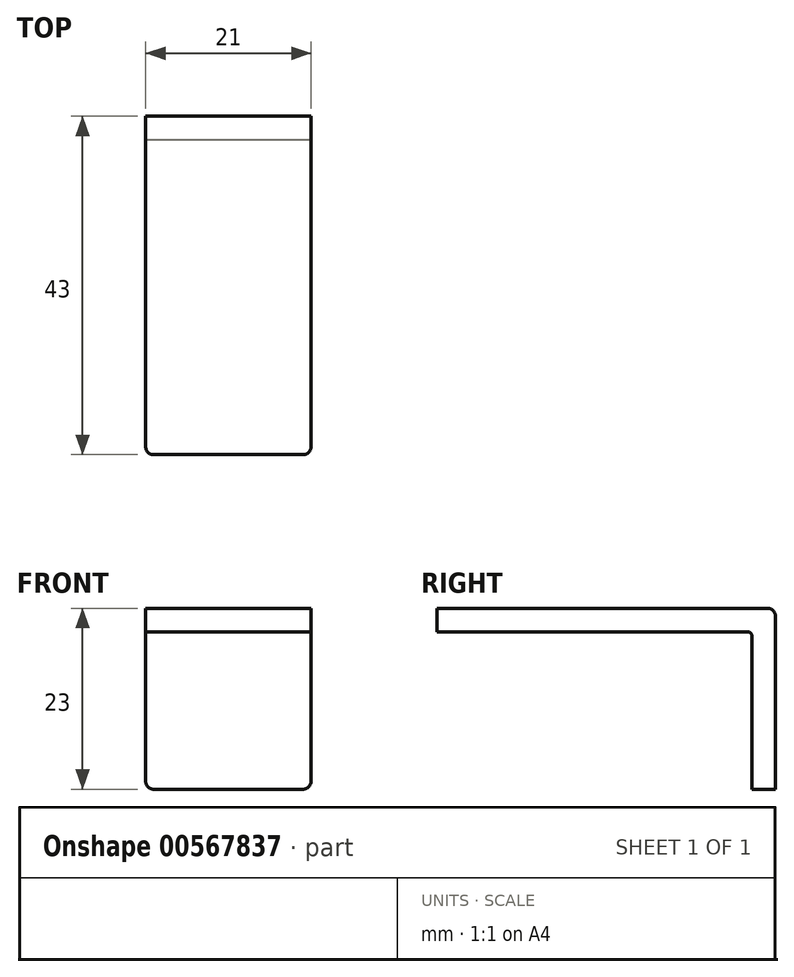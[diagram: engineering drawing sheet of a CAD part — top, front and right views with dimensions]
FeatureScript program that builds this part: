
annotation { "Feature Type Name" : "Feature", "Feature Type Description" : "" }
export const myFeature = defineFeature(function(context is Context, id is Id, definition is map)
    precondition{}
    {
        {
            var Q0;
            Q0=qCreatedBy(makeId("Right.planeOp"),FACE);
            var sketch = newSketch(context, id + "F0", { "sketchPlane" : qUnion([Q0])});
            skLineSegment(sketch, "E0", {"start": v(-40, 0) * mm, "end": v(0, 0) * mm});
            skLineSegment(sketch, "E1", {"start": v(0, 0) * mm, "end": v(0, -20) * mm});
            skLineSegment(sketch, "E2.0", {"start": v(3, 3) * mm, "end": v(3, -20) * mm});
            skLineSegment(sketch, "E2.1", {"start": v(-40, 3) * mm, "end": v(3, 3) * mm});
            skLineSegment(sketch, "E3", {"start": v(-40, 0) * mm, "end": v(-40, 3) * mm});
            skLineSegment(sketch, "E4", {"start": v(0, -20) * mm, "end": v(3, -20) * mm});
            skSolve(sketch);
        }
        {
            var Q0;
            Q0 = qSketchRegion(id + "F0", true);
            extrude(context, id + "F1", {"entities" : qUnion([Q0]), "depth" : 21 * mm, "offsetDistance" : 25 * mm});
        }
        {
            var Q0;
            Q0=makeQuery(id+"F1.opExtrude","SWEPT_EDGE",EDGE,{"disambiguationData":[OSD([sQuery(id+"F0.wireOp",EDGE,"E2.0"),sQuery(id+"F0.wireOp",EDGE,"E2.1")])]});
            var Q1;
            Q1=makeQuery(id+"F1.opExtrude","CAP_EDGE",EDGE,{"disambiguationData":[OSD([sQuery(id+"F0.wireOp",EDGE,"E3")])],"isStart":false});
            var Q2;
            Q2=makeQuery(id+"F1.opExtrude","CAP_EDGE",EDGE,{"disambiguationData":[OSD([sQuery(id+"F0.wireOp",EDGE,"E3")])],"isStart":true});
            var Q3;
            Q3=makeQuery(id+"F1.opExtrude","CAP_EDGE",EDGE,{"disambiguationData":[OSD([sQuery(id+"F0.wireOp",EDGE,"E4")])],"isStart":false});
            var Q4;
            Q4=makeQuery(id+"F1.opExtrude","CAP_EDGE",EDGE,{"disambiguationData":[OSD([sQuery(id+"F0.wireOp",EDGE,"E4")])],"isStart":true});
            fillet(context, id + "F2", {"entities" : qUnion([Q0, Q1, Q2, Q3, Q4]), "radius" : 1 * mm, "tangentPropagation" : true, "allowEdgeOverflow" : false});
        }
        {
            var Q0;
            Q0=makeQuery(id+"F1.opExtrude","SWEPT_EDGE",EDGE,{"disambiguationData":[OSD([sQuery(id+"F0.wireOp",EDGE,"E0"),sQuery(id+"F0.wireOp",EDGE,"E1")])]});
            fillet(context, id + "F3", {"entities" : qUnion([Q0]), "radius" : 0.5 * mm, "tangentPropagation" : true, "allowEdgeOverflow" : false});
        }
    });
